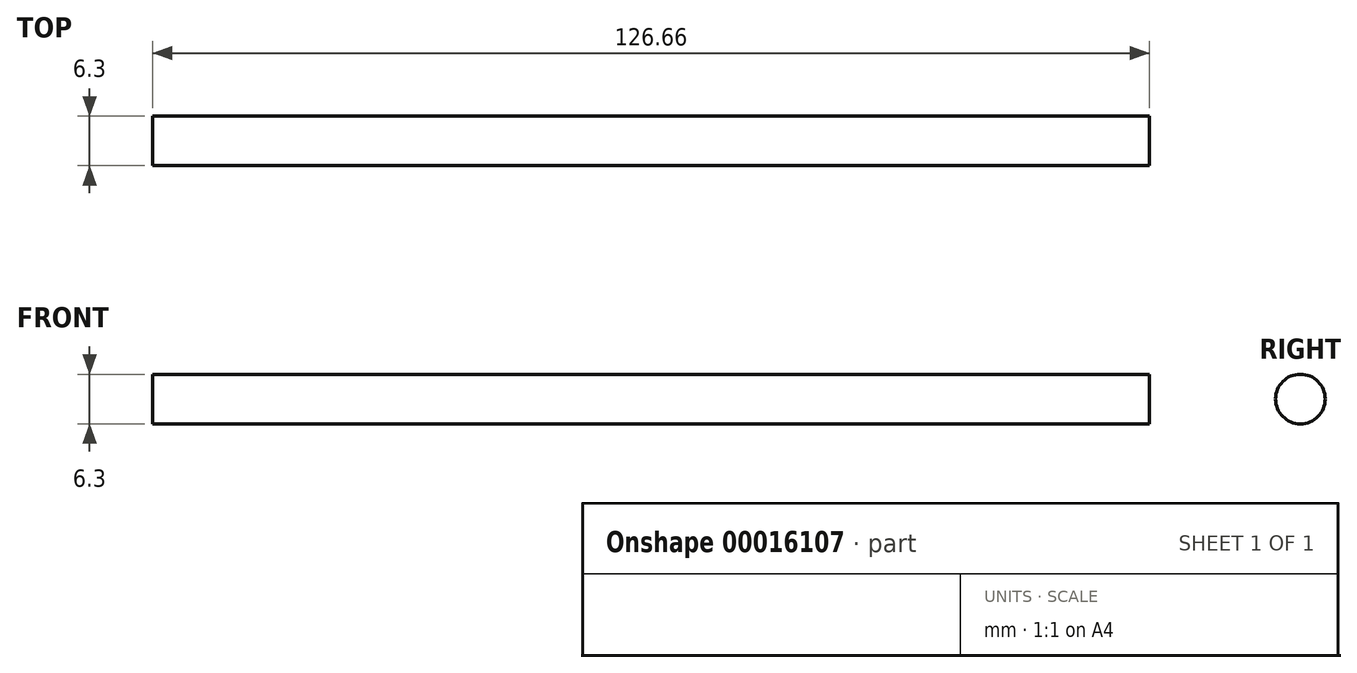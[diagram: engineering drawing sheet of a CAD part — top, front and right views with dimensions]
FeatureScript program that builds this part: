
annotation { "Feature Type Name" : "Feature", "Feature Type Description" : "" }
export const myFeature = defineFeature(function(context is Context, id is Id, definition is map)
    precondition{}
    {
        {
            var Q0;
            Q0=qCreatedBy(makeId("Right.planeOp"),FACE);
            var sketch = newSketch(context, id + "F0", { "sketchPlane" : qUnion([Q0])});
            skCircle(sketch, "E0", {"center": v(0, 0) * mm, "radius": 3.15 * mm});
            skSolve(sketch);
        }
        {
            var Q0;
            Q0=makeQuery(id+"F0.imprint","IMPRINT",FACE,{"disambiguationData":[TD([[makeQuery(id+"F0.imprint","IMPRINT",EDGE,{"derivedFrom":sQuery(id+"F0.wireOp",EDGE,"E0")}),1.0]])]});
            extrude(context, id + "F1", {"entities" : qUnion([Q0]), "depth" : 126.66 * mm});
        }
    });
